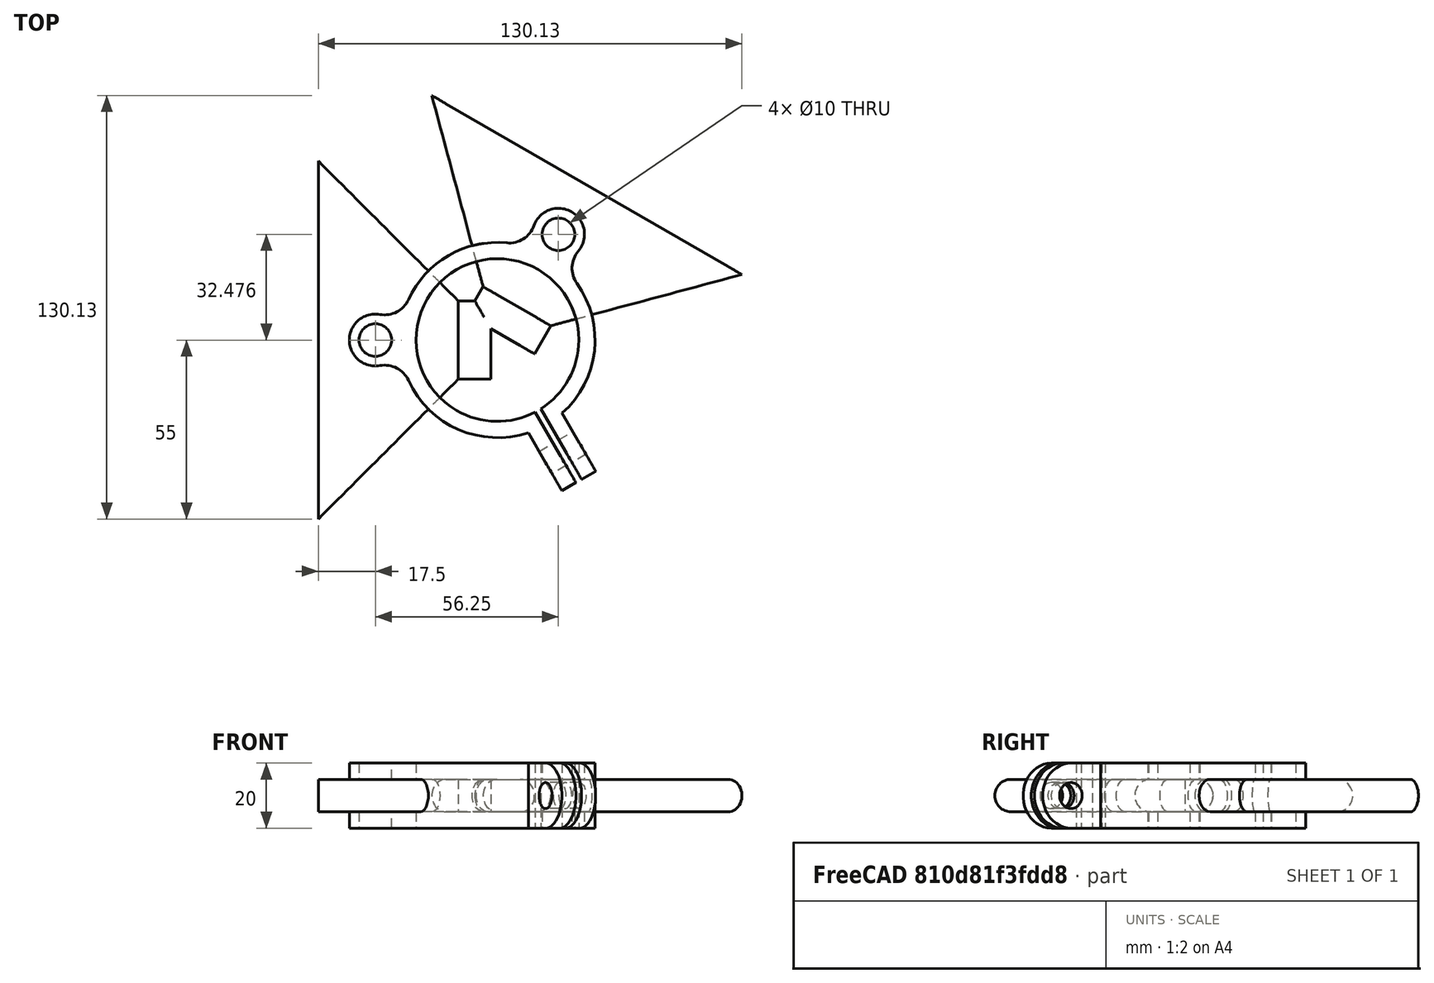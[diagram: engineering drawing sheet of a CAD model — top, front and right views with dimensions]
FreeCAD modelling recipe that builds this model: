
FCSTD DOCUMENT  (FreeCAD 1.0R39319 (Git))
Label: Mania2015-S2
License: All rights reserved
LicenseURL: https://en.wikipedia.org/wiki/All_rights_reserved
objects: Sketcher::SketchObject×7, PartDesign::Pad×3, PartDesign::PolarPattern×2, PartDesign::Body×2, PartDesign::SubShapeBinder×1, PartDesign::AdditiveLoft×1, PartDesign::Boolean×1, PartDesign::Pocket×1
note: 38 computed .brp shape members not serialized (recipe doc carries the construction recipe); baked Part::Feature solids carry a one-line shape summary decoded from their .brp

FEATURE [Sketcher::SketchObject] Sketch
  ArcFitTolerance = 1e-06
  AttachmentSupport = -> [XY_Plane]
  FullyConstrained = true
  MakeInternals = false
  MapMode = 5
  sketch-geometry (7):
    g0: Circle [constr] CenterX=0 CenterY=0 CenterZ=0 NormalX=0 NormalY=0 NormalZ=1 AngleXU=0 Radius=37.5
    g1: ArcOfCircle CenterX=0 CenterY=0 CenterZ=0 NormalX=0 NormalY=0 NormalZ=1 AngleXU=0 Radius=30 StartAngle=3.56847 EndAngle=8.9979
    g2: ArcOfCircle CenterX=-34.59 CenterY=15.7331 CenterZ=0 NormalX=0 NormalY=0 NormalZ=1 AngleXU=0 Radius=8 StartAngle=4.5295 EndAngle=5.85631
    g3: ArcOfCircle CenterX=-34.59 CenterY=-15.7331 CenterZ=0 NormalX=0 NormalY=0 NormalZ=1 AngleXU=0 Radius=8 StartAngle=0.426877 EndAngle=1.75369
    g4: ArcOfCircle CenterX=-37.5 CenterY=0 CenterZ=0 NormalX=0 NormalY=0 NormalZ=1 AngleXU=0 Radius=8 StartAngle=1.3879 EndAngle=4.89528
    g5: Circle CenterX=0 CenterY=0 CenterZ=0 NormalX=0 NormalY=0 NormalZ=1 AngleXU=0 Radius=25
    g6: Circle CenterX=-37.5 CenterY=0 CenterZ=0 NormalX=0 NormalY=0 NormalZ=1 AngleXU=0 Radius=5
  constraints (18):
    c: Diameter(g0) = 75
    c: Diameter(g1) = 60
    c: Coincident(g0,g-1)
    c: Coincident(g1,g0)
    c: Radius(g4) = 8
    c: Tangent(g4,g2) = 1.5708
    c: Tangent(g4,g3) = 1.5708
    c: Equal(g4,g2)
    c: Equal(g4,g3)
    c: PointOnObject(g4,g-1)
    c: PointOnObject(g4,g0)
    c: Tangent(g2,g1) = 1.5708
    c: Tangent(g3,g1) = 1.5708
    c: Diameter(g5) = 50
    c: Diameter(g6) = 10
    c: PointOnObject(g6,g-1)
    c: PointOnObject(g6,g0)
    c: Coincident(g5,g0)
FEATURE [PartDesign::Pad] Pad
  Direction = (0,0,1)
  Length = 20
  Length2 = 10
  Midplane = true
  Profile = -> Sketch
  ReferenceAxis = -> Sketch [N_Axis]
  Refine = true
  Suppressed = false
  Type = 0
FEATURE [Sketcher::SketchObject] Sketch001
  ArcFitTolerance = 1e-06
  AttachmentSupport = -> [XY_Plane]
  FullyConstrained = true
  MakeInternals = false
  MapMode = 5
  sketch-geometry (4):
    g0: LineSegment StartX=-55 StartY=55 StartZ=0 EndX=-55 EndY=-55 EndZ=0
    g1: LineSegment StartX=-55 StartY=-55 StartZ=0 EndX=-12 EndY=-12 EndZ=0
    g2: LineSegment StartX=-12 StartY=12 StartZ=0 EndX=-55 EndY=55 EndZ=0
    g3: LineSegment StartX=-12 StartY=12 StartZ=0 EndX=-12 EndY=-12 EndZ=0
  constraints (10):
    c: Coincident(g0,g1)
    c: Distance(g-2,g0) = 55
    c: Coincident(g2,g0)
    c: Angle(g2,g-1) = 0.785398
    c: Coincident(g3,g2)
    c: Coincident(g3,g1)
    c: Symmetric(g2,g1,g-1)
    c: DistanceY(g3,g3) = 24
    c: DistanceX(g2,g-1) = 12
    c: Symmetric(g0,g0,g-1)
FEATURE [PartDesign::SubShapeBinder] Binder001
  BindCopyOnChange = 0
  BindMode = 0
  ClaimChildren = false
  Context = -> Body [Boolean.Body001.Binder001.]
  Fuse = false
  MakeFace = true
  OffsetFill = false
  OffsetIntersection = false
  OffsetJoinType = 0
  OffsetOpenResult = false
  PartialLoad = false
  Refine = true
  Relative = true
  Support = -> [Body[Sketch001.]]
  _Version = 2
FEATURE [Sketcher::SketchObject] Sketch003
  ArcFitTolerance = 1e-06
  AttachmentOffset = pos=(0,0,-55) rot=(0,0,1;0rad)
  AttachmentSupport = -> [YZ_Plane001]
  ExternalGeometry = -> [Binder001]
  FullyConstrained = true
  MakeInternals = false
  MapMode = 5
  Placement = pos=(-55,0,0) rot=(0.57735,0.57735,0.57735;2.0944rad)
  sketch-geometry (4):
    g0: ArcOfCircle CenterX=-50 CenterY=0 CenterZ=0 NormalX=0 NormalY=0 NormalZ=1 AngleXU=0 Radius=5 StartAngle=1.5708 EndAngle=4.71239
    g1: ArcOfCircle CenterX=50 CenterY=0 CenterZ=0 NormalX=0 NormalY=0 NormalZ=1 AngleXU=0 Radius=5 StartAngle=4.71239 EndAngle=7.85398
    g2: LineSegment StartX=-50 StartY=5 StartZ=0 EndX=50 EndY=5 EndZ=0
    g3: LineSegment StartX=-50 StartY=-5 StartZ=0 EndX=50 EndY=-5 EndZ=0
  constraints (10):
    c: Tangent(g0,g2) = 1.5708
    c: Tangent(g0,g3) = -1.5708
    c: Tangent(g1,g2) = 1.5708
    c: Tangent(g1,g3) = -1.5708
    c: Equal(g0,g1)
    c: Radius(g1) = 5
    c: PointOnObject(g0,g-3)
    c: PointOnObject(g-3,g0)
    c: PointOnObject(g1,g-3)
    c: PointOnObject(g-3,g1)
FEATURE [Sketcher::SketchObject] Sketch004
  ArcFitTolerance = 1e-06
  FullyConstrained = true
  MakeInternals = false
  MapMode = 5
  Placement = pos=(-12,0,-5.3e-15) rot=(0.57735,0.57735,0.57735;2.0944rad)
  sketch-geometry (4):
    g0: ArcOfCircle CenterX=-7 CenterY=0 CenterZ=0 NormalX=0 NormalY=0 NormalZ=1 AngleXU=0 Radius=5 StartAngle=1.5708 EndAngle=4.71239
    g1: ArcOfCircle CenterX=7 CenterY=0 CenterZ=0 NormalX=0 NormalY=0 NormalZ=1 AngleXU=0 Radius=5 StartAngle=4.71239 EndAngle=7.85398
    g2: LineSegment StartX=-7 StartY=5 StartZ=0 EndX=7 EndY=5 EndZ=0
    g3: LineSegment StartX=-7 StartY=-5 StartZ=0 EndX=7 EndY=-5 EndZ=0
  constraints (10):
    c: Tangent(g0,g2) = 1.5708
    c: Tangent(g0,g3) = -1.5708
    c: Tangent(g1,g2) = 1.5708
    c: Tangent(g1,g3) = -1.5708
    c: Equal(g0,g1)
    c: Radius(g1) = 5
    c: PointOnObject(g1,g-1)
    c: PointOnObject(g0,g-1)
    c: PointOnObject(g-3,g1)
    c: PointOnObject(g-4,g0)
FEATURE [Sketcher::SketchObject] Sketch005
  ArcFitTolerance = 1e-06
  FullyConstrained = true
  MakeInternals = false
  MapMode = 5
  Placement = pos=(-12,0,-5.3e-15) rot=(0.57735,0.57735,0.57735;2.0944rad)
  sketch-geometry (4):
    g0: ArcOfCircle CenterX=-7 CenterY=0 CenterZ=0 NormalX=0 NormalY=0 NormalZ=1 AngleXU=0 Radius=5 StartAngle=1.5708 EndAngle=4.71239
    g1: ArcOfCircle CenterX=7 CenterY=0 CenterZ=0 NormalX=0 NormalY=0 NormalZ=1 AngleXU=0 Radius=5 StartAngle=4.71239 EndAngle=7.85398
    g2: LineSegment StartX=-7 StartY=5 StartZ=0 EndX=7 EndY=5 EndZ=0
    g3: LineSegment StartX=-7 StartY=-5 StartZ=0 EndX=7 EndY=-5 EndZ=0
  constraints (10):
    c: Tangent(g0,g2) = 1.5708
    c: Tangent(g0,g3) = -1.5708
    c: Tangent(g1,g2) = 1.5708
    c: Tangent(g1,g3) = -1.5708
    c: Equal(g0,g1)
    c: Radius(g1) = 5
    c: PointOnObject(g1,g-1)
    c: PointOnObject(g0,g-1)
    c: PointOnObject(g-3,g1)
    c: PointOnObject(g-4,g0)
FEATURE [PartDesign::AdditiveLoft] AdditiveLoft
  Closed = false
  Placement = pos=(-12,0,-5.3e-15) rot=(0.57735,0.57735,0.57735;2.0944rad)
  Profile = -> Sketch004
  Refine = true
  Ruled = false
  Sections = -> [Sketch003]
  Suppressed = false
FEATURE [PartDesign::Pad] Pad001
  BaseFeature = -> AdditiveLoft
  Direction = (1,1e-16,-1e-16)
  Length = 10
  Length2 = 10
  Placement = pos=(-12,0,-5.3e-15) rot=(0.57735,0.57735,0.57735;2.0944rad)
  Profile = -> Sketch005
  ReferenceAxis = -> Sketch005 [N_Axis]
  Refine = true
  Suppressed = false
  Type = 0
FEATURE [PartDesign::PolarPattern] PolarPattern001
  Angle = 360
  Axis = -> Z_Axis001
  BaseFeature = -> Pad001
  Mode = 1
  Occurrences = 2
  Offset = 120
  Originals = -> [Pad001]
  Placement = pos=(-12,0,-5.3e-15) rot=(0.57735,0.57735,0.57735;2.0944rad)
  Refine = true
  Reversed = true
  Suppressed = false
  TransformMode = 1
FEATURE [PartDesign::Body] Body001
  AllowCompound = false
  Group = -> [Binder001,Sketch003,Sketch004,Sketch005,AdditiveLoft,Pad001,PolarPattern001]
  Origin = -> Origin001
  Tip = -> PolarPattern001
FEATURE [Sketcher::SketchObject] Sketch006
  ArcFitTolerance = 1e-06
  AttachmentOffset = pos=(0,0,0) rot=(0,1,0;0.523599rad)
  AttachmentSupport = -> [YZ_Plane]
  ExternalGeometry = -> [Pad]
  FullyConstrained = true
  MakeInternals = false
  MapMode = 5
  Placement = pos=(0,0,0) rot=(0.377964,0.654654,0.654654;2.41886rad)
  sketch-geometry (5):
    g0: LineSegment StartX=-25 StartY=-10 StartZ=0 EndX=-25 EndY=10 EndZ=0
    g1: LineSegment StartX=-25 StartY=10 StartZ=0 EndX=-40 EndY=10 EndZ=0
    g2: LineSegment StartX=-40 StartY=-10 StartZ=0 EndX=-25 EndY=-10 EndZ=0
    g3: ArcOfCircle CenterX=-40 CenterY=0 CenterZ=0 NormalX=0 NormalY=0 NormalZ=1 AngleXU=0 Radius=10 StartAngle=1.5708 EndAngle=4.71239
    g4: Circle CenterX=-40 CenterY=0 CenterZ=0 NormalX=0 NormalY=0 NormalZ=1 AngleXU=0 Radius=4
  constraints (13):
    c: Coincident(g0,g1)
    c: Coincident(g2,g0)
    c: Vertical(g0)
    c: Horizontal(g1)
    c: Horizontal(g2)
    c: PointOnObject(g-3,g1)
    c: PointOnObject(g3,g-1)
    c: Tangent(g3,g1) = -1.5708
    c: Tangent(g3,g2) = -1.5708
    c: Distance(g3,g-1) = 40
    c: Diameter(g4) = 8
    c: Coincident(g4,g3)
    c: DistanceX(g2,g2) = 15
FEATURE [PartDesign::PolarPattern] PolarPattern
  Angle = 120
  Axis = -> Sketch [N_Axis]
  BaseFeature = -> Pad
  Mode = 1
  Occurrences = 2
  Offset = 120
  Originals = -> [Pad]
  Refine = true
  Reversed = true
  Suppressed = false
  TransformMode = 0
FEATURE [PartDesign::Pad] Pad002
  BaseFeature = -> PolarPattern
  Direction = (0.866025,0.5,0)
  Length = 12
  Length2 = 10
  Midplane = true
  Profile = -> Sketch006
  ReferenceAxis = -> Sketch006 [N_Axis]
  Refine = true
  Suppressed = false
  Type = 0
FEATURE [PartDesign::Boolean] Boolean
  BaseFeature = -> Pad002
  Group = -> [Body001]
  Refine = true
  Suppressed = false
  Type = 1
  UsePlacement = true
FEATURE [Sketcher::SketchObject] Sketch007
  ArcFitTolerance = 1e-06
  AttachmentSupport = -> [XY_Plane]
  FullyConstrained = true
  MakeInternals = false
  MapMode = 5
  sketch-geometry (5):
    g0: LineSegment [constr] StartX=0 StartY=0 StartZ=0 EndX=40.4145 EndY=-70 EndZ=0
    g1: LineSegment StartX=9.80341 StartY=-18.98 StartZ=0 EndX=11.5355 EndY=-17.98 EndZ=0
    g2: LineSegment StartX=11.5355 StartY=-17.98 StartZ=0 EndX=32.5355 EndY=-54.3531 EndZ=0
    g3: LineSegment StartX=32.5355 StartY=-54.3531 StartZ=0 EndX=30.8034 EndY=-55.3531 EndZ=0
    g4: LineSegment StartX=30.8034 StartY=-55.3531 StartZ=0 EndX=9.80341 EndY=-18.98 EndZ=0
  constraints (14):
    c: Coincident(g0,g-1)
    c: Angle(g-1,g0) = 2.0944
    c: DistanceY(g0,g0) = 70
    c: Coincident(g1,g2)
    c: Coincident(g2,g3)
    c: Coincident(g3,g4)
    c: Coincident(g4,g1)
    c: Parallel(g2,g0)
    c: Parallel(g4,g0)
    c: Perpendicular(g2,g1)
    c: Symmetric(g2,g3,g0)
    c: Distance(g3,g3) = 2
    c: Distance(g4,g4) = 42
    c: DistanceY(g1,g-1) = 18.98
FEATURE [PartDesign::Pocket] Pocket
  BaseFeature = -> Boolean
  Direction = (0,0,-1)
  Length = 5
  Length2 = 5
  Midplane = true
  Profile = -> Sketch007
  ReferenceAxis = -> Sketch007 [N_Axis]
  Refine = true
  Suppressed = false
  Type = 1
FEATURE [PartDesign::Body] Body
  AllowCompound = false
  Group = -> [Sketch,Pad,Sketch001,Sketch006,PolarPattern,Pad002,Boolean,Sketch007,Pocket]
  Origin = -> Origin
  Tip = -> Pocket
